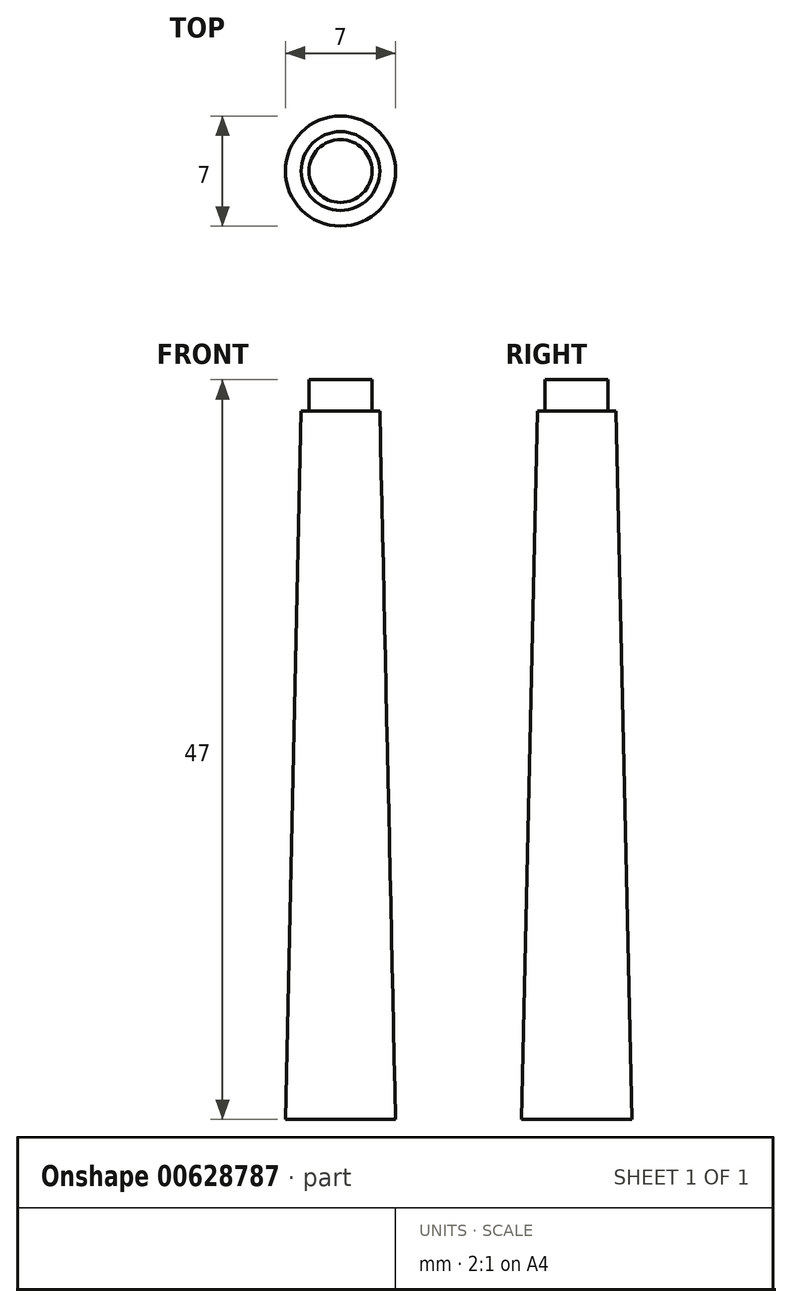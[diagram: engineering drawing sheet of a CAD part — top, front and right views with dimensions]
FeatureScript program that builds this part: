
annotation { "Feature Type Name" : "Feature", "Feature Type Description" : "" }
export const myFeature = defineFeature(function(context is Context, id is Id, definition is map)
    precondition{}
    {
        {
            var Q0;
            Q0=qCreatedBy(makeId("Top.planeOp"),FACE);
            cPlane(context, id + "F0", {"entities" : qUnion([Q0]), "cplaneType" : CPlaneType.OFFSET, "offset" : 45 * mm, "width" : 150 * mm, "height" : 150 * mm});
        }
        {
            var Q0;
            Q0=qCreatedBy(makeId("Top.planeOp"),FACE);
            var sketch = newSketch(context, id + "F1", { "sketchPlane" : qUnion([Q0])});
            skCircle(sketch, "E0", {"center": v(0, 0) * mm, "radius": 3.5 * mm});
            skSolve(sketch);
        }
        {
            var Q0;
            Q0=qCreatedBy(id+"F0.planeOp",FACE);
            var sketch = newSketch(context, id + "F2", { "sketchPlane" : qUnion([Q0])});
            skCircle(sketch, "E1", {"center": v(0, 0) * mm, "radius": 2.5 * mm});
            skSolve(sketch);
        }
        {
            var Q0;
            Q0 = qSketchRegion(id + "F1", true);
            var Q1;
            Q1 = qSketchRegion(id + "F2", true);
            loft(context, id + "F3", {"sheetProfilesArray" : [{ "sheetProfileEntities" : qUnion([Q0]) }, { "sheetProfileEntities" : qUnion([Q1]) }]});
        }
        {
            var Q0;
            Q0=qCreatedBy(id+"F0.planeOp",FACE);
            var sketch = newSketch(context, id + "F4", { "sketchPlane" : qUnion([Q0])});
            skCircle(sketch, "E2", {"center": v(0, 0) * mm, "radius": 2 * mm});
            skSolve(sketch);
        }
        {
            var Q0;
            Q0=makeQuery(id+"F4.imprint","IMPRINT",FACE,{"disambiguationData":[TD([[makeQuery(id+"F4.imprint","IMPRINT",EDGE,{"derivedFrom":sQuery(id+"F4.wireOp",EDGE,"E2")}),1.0]])]});
            extrude(context, id + "F5", {"entities" : qUnion([Q0]), "operationType" : NewBodyOperationType.ADD, "depth" : 2 * mm, "offsetDistance" : 25 * mm});
        }
    });
